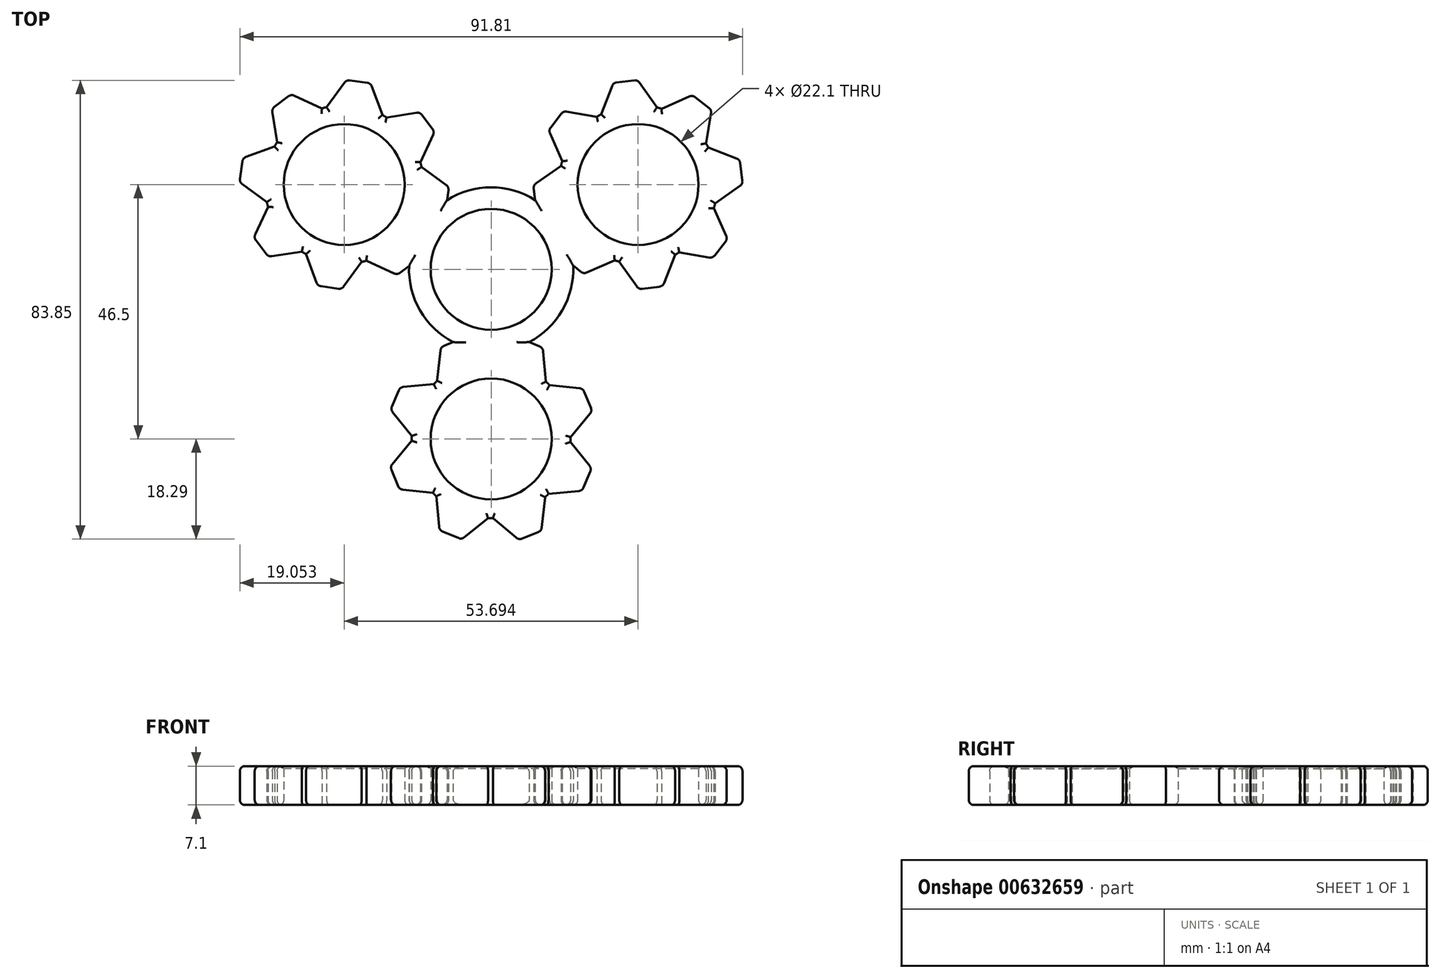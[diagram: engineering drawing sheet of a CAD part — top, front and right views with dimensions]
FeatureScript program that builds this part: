
annotation { "Feature Type Name" : "Feature", "Feature Type Description" : "" }
export const myFeature = defineFeature(function(context is Context, id is Id, definition is map)
    precondition{}
    {
        {
            var Q0;
            Q0=qCreatedBy(makeId("Top.planeOp"),FACE);
            var sketch = newSketch(context, id + "F0", { "sketchPlane" : qUnion([Q0])});
            skCircle(sketch, "E0", {"center": v(0, 0) * mm, "radius": 11.05 * mm});
            skArc(sketch, "E1", {"start": v(6.93, -13.3) * mm, "mid": v(13, -7.5) * mm, "end": v(14.99, 0.66) * mm});
            skCircle(sketch, "E2", {"center": v(0, -31) * mm, "radius": 11.05 * mm});
            skLineSegment(sketch, "E3", {"start": v(0, -31) * mm, "end": v(7.42, -13.5) * mm, "construction": true});
            skLineSegment(sketch, "E4", {"start": v(10.02, -20.52) * mm, "end": v(9.51, -14.97) * mm});
            skLineSegment(sketch, "E5", {"start": v(0, 0) * mm, "end": v(0, -31) * mm, "construction": true});
            skArc(sketch, "E6", {"start": v(-9.85, -20.36) * mm, "mid": v(-10.17, -20.66) * mm, "end": v(-10.48, -20.98) * mm});
            skLineSegment(sketch, "E7", {"start": v(7.42, -13.5) * mm, "end": v(8.9, -14.14) * mm});
            skLineSegment(sketch, "E8.MirrorCS", {"start": v(7.42, -13.5) * mm, "end": v(6.93, -13.3) * mm});
            skPoint(sketch, "E9.visualSharp", {"position": v(5.37, -12.64) * mm});
            skPoint(sketch, "E10.visualSharp", {"position": v(9.46, -14.37) * mm});
            skArc(sketch, "E10.filletArc", {"start": v(9.51, -14.97) * mm, "mid": v(9.32, -14.47) * mm, "end": v(8.9, -14.14) * mm});
            skLineSegment(sketch, "E11.1.2", {"start": v(-7.13, -13.39) * mm, "end": v(-6.93, -13.3) * mm});
            skLineSegment(sketch, "E11.1.3", {"start": v(-7.13, -13.39) * mm, "end": v(-8.63, -14) * mm});
            skArc(sketch, "E11.1.4", {"start": v(-8.63, -14) * mm, "mid": v(-9.05, -14.32) * mm, "end": v(-9.25, -14.81) * mm});
            skLineSegment(sketch, "E11.1.5", {"start": v(-9.85, -20.36) * mm, "end": v(-9.25, -14.81) * mm});
            skLineSegment(sketch, "E11.2.0", {"start": v(-10.48, -20.98) * mm, "end": v(-16.03, -21.49) * mm});
            skArc(sketch, "E11.2.1", {"start": v(-16.03, -21.49) * mm, "mid": v(-16.53, -21.68) * mm, "end": v(-16.86, -22.1) * mm});
            skLineSegment(sketch, "E11.2.2", {"start": v(-17.5, -23.58) * mm, "end": v(-16.86, -22.1) * mm});
            skLineSegment(sketch, "E11.2.3", {"start": v(-17.5, -23.58) * mm, "end": v(-18.12, -25.07) * mm});
            skArc(sketch, "E11.2.4", {"start": v(-18.12, -25.07) * mm, "mid": v(-18.2, -25.6) * mm, "end": v(-17.98, -26.1) * mm});
            skLineSegment(sketch, "E11.2.5", {"start": v(-14.49, -30.44) * mm, "end": v(-17.98, -26.1) * mm});
            skLineSegment(sketch, "E11.3.0", {"start": v(-14.5, -31.32) * mm, "end": v(-18.06, -35.61) * mm});
            skArc(sketch, "E11.3.1", {"start": v(-18.06, -35.61) * mm, "mid": v(-18.28, -36.1) * mm, "end": v(-18.22, -36.62) * mm});
            skLineSegment(sketch, "E11.3.2", {"start": v(-17.61, -38.13) * mm, "end": v(-18.22, -36.62) * mm});
            skLineSegment(sketch, "E11.3.3", {"start": v(-17.61, -38.13) * mm, "end": v(-17, -39.63) * mm});
            skArc(sketch, "E11.3.4", {"start": v(-17, -39.63) * mm, "mid": v(-16.68, -40.05) * mm, "end": v(-16.19, -40.25) * mm});
            skLineSegment(sketch, "E11.3.5", {"start": v(-10.64, -40.85) * mm, "end": v(-16.19, -40.25) * mm});
            skLineSegment(sketch, "E11.4.0", {"start": v(-10.02, -41.48) * mm, "end": v(-9.51, -47.03) * mm});
            skArc(sketch, "E11.4.1", {"start": v(-9.51, -47.03) * mm, "mid": v(-9.32, -47.53) * mm, "end": v(-8.9, -47.86) * mm});
            skLineSegment(sketch, "E11.4.2", {"start": v(-7.42, -48.5) * mm, "end": v(-8.9, -47.86) * mm});
            skLineSegment(sketch, "E11.4.3", {"start": v(-7.42, -48.5) * mm, "end": v(-5.93, -49.12) * mm});
            skArc(sketch, "E11.4.4", {"start": v(-5.93, -49.12) * mm, "mid": v(-5.4, -49.2) * mm, "end": v(-4.9, -48.98) * mm});
            skLineSegment(sketch, "E11.4.5", {"start": v(-0.56, -45.49) * mm, "end": v(-4.9, -48.98) * mm});
            skLineSegment(sketch, "E11.5.0", {"start": v(0.32, -45.5) * mm, "end": v(4.61, -49.06) * mm});
            skArc(sketch, "E11.5.1", {"start": v(4.61, -49.06) * mm, "mid": v(5.1, -49.28) * mm, "end": v(5.62, -49.22) * mm});
            skLineSegment(sketch, "E11.5.2", {"start": v(7.13, -48.61) * mm, "end": v(5.62, -49.22) * mm});
            skLineSegment(sketch, "E11.5.3", {"start": v(7.13, -48.61) * mm, "end": v(8.63, -48) * mm});
            skArc(sketch, "E11.5.4", {"start": v(8.63, -48) * mm, "mid": v(9.05, -47.68) * mm, "end": v(9.25, -47.19) * mm});
            skLineSegment(sketch, "E11.5.5", {"start": v(9.85, -41.64) * mm, "end": v(9.25, -47.19) * mm});
            skLineSegment(sketch, "E11.6.0", {"start": v(10.48, -41.02) * mm, "end": v(16.03, -40.51) * mm});
            skArc(sketch, "E11.6.1", {"start": v(16.03, -40.51) * mm, "mid": v(16.53, -40.32) * mm, "end": v(16.86, -39.9) * mm});
            skLineSegment(sketch, "E11.6.2", {"start": v(17.5, -38.42) * mm, "end": v(16.86, -39.9) * mm});
            skLineSegment(sketch, "E11.6.3", {"start": v(17.5, -38.42) * mm, "end": v(18.12, -36.93) * mm});
            skArc(sketch, "E11.6.4", {"start": v(18.12, -36.93) * mm, "mid": v(18.2, -36.4) * mm, "end": v(17.98, -35.9) * mm});
            skLineSegment(sketch, "E11.6.5", {"start": v(14.49, -31.56) * mm, "end": v(17.98, -35.9) * mm});
            skLineSegment(sketch, "E11.7.0", {"start": v(14.5, -30.68) * mm, "end": v(18.06, -26.39) * mm});
            skArc(sketch, "E11.7.1", {"start": v(18.06, -26.39) * mm, "mid": v(18.28, -25.9) * mm, "end": v(18.22, -25.38) * mm});
            skLineSegment(sketch, "E11.7.2", {"start": v(17.61, -23.87) * mm, "end": v(18.22, -25.38) * mm});
            skLineSegment(sketch, "E11.7.3", {"start": v(17.61, -23.87) * mm, "end": v(17, -22.37) * mm});
            skArc(sketch, "E11.7.4", {"start": v(17, -22.37) * mm, "mid": v(16.68, -21.95) * mm, "end": v(16.19, -21.75) * mm});
            skLineSegment(sketch, "E11.7.5", {"start": v(10.64, -21.15) * mm, "end": v(16.19, -21.75) * mm});
            skPoint(sketch, "E12.orphan", {"position": v(0.56, -16.51) * mm});
            skPoint(sketch, "E13.orphan", {"position": v(-0.32, -16.5) * mm});
            skArc(sketch, "E14.trimOffspring", {"start": v(10.64, -21.15) * mm, "mid": v(10.34, -20.83) * mm, "end": v(10.02, -20.52) * mm});
            skArc(sketch, "E15.trimOffspring", {"start": v(14.49, -31.56) * mm, "mid": v(14.5, -31.12) * mm, "end": v(14.5, -30.68) * mm});
            skArc(sketch, "E16.trimOffspring", {"start": v(9.85, -41.64) * mm, "mid": v(10.17, -41.34) * mm, "end": v(10.48, -41.02) * mm});
            skArc(sketch, "E17.trimOffspring", {"start": v(-0.56, -45.49) * mm, "mid": v(-0.12, -45.5) * mm, "end": v(0.32, -45.5) * mm});
            skArc(sketch, "E18.trimOffspring", {"start": v(-10.64, -40.85) * mm, "mid": v(-10.34, -41.17) * mm, "end": v(-10.02, -41.48) * mm});
            skArc(sketch, "E19.trimOffspring", {"start": v(-14.49, -30.44) * mm, "mid": v(-14.5, -30.88) * mm, "end": v(-14.5, -31.32) * mm});
            skLineSegment(sketch, "E20.1.0", {"start": v(22.55, 1.65) * mm, "end": v(17.45, -0.6) * mm});
            skPoint(sketch, "E20.1.1", {"position": v(7.72, 15.38) * mm});
            skLineSegment(sketch, "E20.1.2", {"start": v(30.29, 29.59) * mm, "end": v(27.07, 34.14) * mm});
            skArc(sketch, "E20.1.3", {"start": v(13, 19.8) * mm, "mid": v(12.87, 19.37) * mm, "end": v(12.76, 18.94) * mm});
            skPoint(sketch, "E20.1.4", {"position": v(26.85, 15.5) * mm});
            skLineSegment(sketch, "E20.1.5", {"start": v(19.32, 27.9) * mm, "end": v(13.82, 28.84) * mm});
            skLineSegment(sketch, "E20.1.7", {"start": v(40.7, 11.2) * mm, "end": v(42.95, 6.1) * mm});
            skPoint(sketch, "E20.1.8", {"position": v(14.02, 8.74) * mm});
            skArc(sketch, "E20.1.9", {"start": v(39.68, 22.26) * mm, "mid": v(39.46, 22.65) * mm, "end": v(39.24, 23.03) * mm});
            skArc(sketch, "E20.1.10", {"start": v(20.09, 28.33) * mm, "mid": v(19.7, 28.12) * mm, "end": v(19.32, 27.9) * mm});
            skLineSegment(sketch, "E20.1.11", {"start": v(31.14, 29.35) * mm, "end": v(36.24, 31.6) * mm});
            skArc(sketch, "E20.1.12", {"start": v(22.55, 1.65) * mm, "mid": v(22.98, 1.53) * mm, "end": v(23.4, 1.41) * mm});
            skLineSegment(sketch, "E20.1.13", {"start": v(23.4, 1.41) * mm, "end": v(26.63, -3.14) * mm});
            skPoint(sketch, "E20.1.14", {"position": v(14.45, 7.97) * mm});
            skArc(sketch, "E20.1.15", {"start": v(31.14, 29.35) * mm, "mid": v(30.72, 29.47) * mm, "end": v(30.29, 29.59) * mm});
            skCircle(sketch, "E20.1.16", {"center": v(26.85, 15.5) * mm, "radius": 11.05 * mm});
            skLineSegment(sketch, "E20.1.18", {"start": v(40.93, 12.06) * mm, "end": v(45.49, 15.28) * mm});
            skLineSegment(sketch, "E20.1.19", {"start": v(13, 19.8) * mm, "end": v(10.75, 24.9) * mm});
            skArc(sketch, "E20.1.20", {"start": v(40.7, 11.2) * mm, "mid": v(40.82, 11.63) * mm, "end": v(40.93, 12.06) * mm});
            skLineSegment(sketch, "E20.1.21", {"start": v(12.76, 18.94) * mm, "end": v(8.2, 15.72) * mm});
            skArc(sketch, "E20.1.22", {"start": v(33.6, 2.67) * mm, "mid": v(34, 2.88) * mm, "end": v(34.38, 3.1) * mm});
            skPoint(sketch, "E20.1.23", {"position": v(26.85, 15.5) * mm});
            skArc(sketch, "E20.1.24", {"start": v(45.49, 15.28) * mm, "mid": v(45.82, 15.7) * mm, "end": v(45.9, 16.22) * mm});
            skArc(sketch, "E20.1.25", {"start": v(10.87, 25.91) * mm, "mid": v(10.67, 25.42) * mm, "end": v(10.75, 24.9) * mm});
            skLineSegment(sketch, "E20.1.26", {"start": v(41.82, 3.8) * mm, "end": v(42.82, 5.09) * mm});
            skArc(sketch, "E20.1.27", {"start": v(42.82, 5.09) * mm, "mid": v(43.02, 5.58) * mm, "end": v(42.95, 6.1) * mm});
            skLineSegment(sketch, "E20.1.28", {"start": v(20.09, 28.33) * mm, "end": v(22.1, 33.53) * mm});
            skLineSegment(sketch, "E20.1.29", {"start": v(34.38, 3.1) * mm, "end": v(39.87, 2.16) * mm});
            skArc(sketch, "E20.1.30", {"start": v(27.07, 34.14) * mm, "mid": v(26.66, 34.48) * mm, "end": v(26.13, 34.56) * mm});
            skLineSegment(sketch, "E20.1.31", {"start": v(33.6, 2.67) * mm, "end": v(31.59, -2.53) * mm});
            skArc(sketch, "E20.1.32", {"start": v(26.63, -3.14) * mm, "mid": v(27.04, -3.48) * mm, "end": v(27.56, -3.56) * mm});
            skLineSegment(sketch, "E20.1.33", {"start": v(29.17, -3.36) * mm, "end": v(27.56, -3.56) * mm});
            skLineSegment(sketch, "E20.1.34", {"start": v(15.16, 0.52) * mm, "end": v(16.43, -0.47) * mm});
            skArc(sketch, "E20.1.35", {"start": v(39.87, 2.16) * mm, "mid": v(40.4, 2.22) * mm, "end": v(40.83, 2.53) * mm});
            skLineSegment(sketch, "E20.1.36", {"start": v(45.7, 17.82) * mm, "end": v(45.5, 19.43) * mm});
            skLineSegment(sketch, "E20.1.37", {"start": v(41.82, 3.8) * mm, "end": v(40.83, 2.53) * mm});
            skLineSegment(sketch, "E20.1.38", {"start": v(29.17, -3.36) * mm, "end": v(30.78, -3.16) * mm});
            skLineSegment(sketch, "E20.1.39", {"start": v(24.52, 34.36) * mm, "end": v(26.13, 34.56) * mm});
            skLineSegment(sketch, "E20.1.40", {"start": v(11.87, 27.2) * mm, "end": v(12.87, 28.47) * mm});
            skArc(sketch, "E20.1.41", {"start": v(45.5, 19.43) * mm, "mid": v(45.3, 19.92) * mm, "end": v(44.88, 20.24) * mm});
            skArc(sketch, "E20.1.42", {"start": v(37.26, 31.47) * mm, "mid": v(36.77, 31.68) * mm, "end": v(36.24, 31.6) * mm});
            skArc(sketch, "E20.1.43", {"start": v(22.92, 34.16) * mm, "mid": v(22.42, 33.96) * mm, "end": v(22.1, 33.53) * mm});
            skLineSegment(sketch, "E20.1.44", {"start": v(45.7, 17.82) * mm, "end": v(45.9, 16.22) * mm});
            skArc(sketch, "E20.1.45", {"start": v(8.2, 15.72) * mm, "mid": v(7.87, 15.3) * mm, "end": v(7.8, 14.78) * mm});
            skLineSegment(sketch, "E20.1.46", {"start": v(39.24, 23.03) * mm, "end": v(40.18, 28.52) * mm});
            skLineSegment(sketch, "E20.1.47", {"start": v(38.54, 30.48) * mm, "end": v(37.26, 31.47) * mm});
            skArc(sketch, "E20.1.48", {"start": v(30.78, -3.16) * mm, "mid": v(31.27, -2.96) * mm, "end": v(31.59, -2.53) * mm});
            skLineSegment(sketch, "E20.1.49", {"start": v(38.54, 30.48) * mm, "end": v(39.81, 29.48) * mm});
            skPoint(sketch, "E20.1.50", {"position": v(8.26, 10.98) * mm});
            skLineSegment(sketch, "E20.1.51", {"start": v(24.52, 34.36) * mm, "end": v(22.92, 34.16) * mm});
            skArc(sketch, "E20.1.53", {"start": v(13.82, 28.84) * mm, "mid": v(13.3, 28.78) * mm, "end": v(12.87, 28.47) * mm});
            skArc(sketch, "E20.1.54", {"start": v(40.18, 28.52) * mm, "mid": v(40.13, 29.05) * mm, "end": v(39.81, 29.48) * mm});
            skArc(sketch, "E20.1.55", {"start": v(16.43, -0.47) * mm, "mid": v(16.92, -0.68) * mm, "end": v(17.45, -0.6) * mm});
            skLineSegment(sketch, "E20.1.56", {"start": v(39.68, 22.26) * mm, "end": v(44.88, 20.24) * mm});
            skLineSegment(sketch, "E20.1.57", {"start": v(11.87, 27.2) * mm, "end": v(10.87, 25.91) * mm});
            skLineSegment(sketch, "E20.1.59", {"start": v(15.16, 0.52) * mm, "end": v(14.99, 0.66) * mm});
            skLineSegment(sketch, "E20.1.62", {"start": v(7.99, 13.18) * mm, "end": v(7.8, 14.78) * mm});
            skLineSegment(sketch, "E20.1.63", {"start": v(7.99, 13.18) * mm, "end": v(8.05, 12.65) * mm});
            skLineSegment(sketch, "E20.2.0", {"start": v(-12.7, 18.7) * mm, "end": v(-8.2, 15.41) * mm});
            skPoint(sketch, "E20.2.1", {"position": v(-17.18, -1) * mm});
            skLineSegment(sketch, "E20.2.2", {"start": v(-40.77, 11.44) * mm, "end": v(-43.1, 6.37) * mm});
            skArc(sketch, "E20.2.3", {"start": v(-23.64, 1.36) * mm, "mid": v(-23.2, 1.46) * mm, "end": v(-22.78, 1.58) * mm});
            skPoint(sketch, "E20.2.4", {"position": v(-26.85, 15.5) * mm});
            skLineSegment(sketch, "E20.2.5", {"start": v(-33.81, 2.78) * mm, "end": v(-31.89, -2.45) * mm});
            skLineSegment(sketch, "E20.2.7", {"start": v(-30.05, 29.64) * mm, "end": v(-26.76, 34.14) * mm});
            skPoint(sketch, "E20.2.8", {"position": v(-14.58, 7.77) * mm});
            skArc(sketch, "E20.2.9", {"start": v(-39.11, 23.23) * mm, "mid": v(-39.34, 22.85) * mm, "end": v(-39.56, 22.47) * mm});
            skArc(sketch, "E20.2.10", {"start": v(-34.58, 3.23) * mm, "mid": v(-34.2, 3) * mm, "end": v(-33.81, 2.78) * mm});
            skLineSegment(sketch, "E20.2.11", {"start": v(-40.99, 12.3) * mm, "end": v(-45.49, 15.59) * mm});
            skArc(sketch, "E20.2.12", {"start": v(-12.7, 18.7) * mm, "mid": v(-12.81, 19.14) * mm, "end": v(-12.93, 19.56) * mm});
            skLineSegment(sketch, "E20.2.13", {"start": v(-12.93, 19.56) * mm, "end": v(-10.6, 24.63) * mm});
            skPoint(sketch, "E20.2.14", {"position": v(-14.13, 8.53) * mm});
            skArc(sketch, "E20.2.15", {"start": v(-40.99, 12.3) * mm, "mid": v(-40.88, 11.86) * mm, "end": v(-40.77, 11.44) * mm});
            skCircle(sketch, "E20.2.16", {"center": v(-26.85, 15.5) * mm, "radius": 11.05 * mm});
            skLineSegment(sketch, "E20.2.18", {"start": v(-30.91, 29.42) * mm, "end": v(-35.97, 31.75) * mm});
            skLineSegment(sketch, "E20.2.19", {"start": v(-23.64, 1.36) * mm, "end": v(-26.93, -3.14) * mm});
            skArc(sketch, "E20.2.20", {"start": v(-30.05, 29.64) * mm, "mid": v(-30.48, 29.54) * mm, "end": v(-30.91, 29.42) * mm});
            skLineSegment(sketch, "E20.2.21", {"start": v(-22.78, 1.58) * mm, "end": v(-17.72, -0.75) * mm});
            skArc(sketch, "E20.2.22", {"start": v(-19.11, 27.77) * mm, "mid": v(-19.5, 28) * mm, "end": v(-19.88, 28.22) * mm});
            skPoint(sketch, "E20.2.23", {"position": v(-26.85, 15.5) * mm});
            skArc(sketch, "E20.2.24", {"start": v(-35.97, 31.75) * mm, "mid": v(-36.5, 31.84) * mm, "end": v(-37, 31.64) * mm});
            skArc(sketch, "E20.2.25", {"start": v(-27.88, -3.54) * mm, "mid": v(-27.35, -3.47) * mm, "end": v(-26.93, -3.14) * mm});
            skLineSegment(sketch, "E20.2.26", {"start": v(-24.21, 34.32) * mm, "end": v(-25.81, 34.54) * mm});
            skArc(sketch, "E20.2.27", {"start": v(-25.81, 34.54) * mm, "mid": v(-26.34, 34.47) * mm, "end": v(-26.76, 34.14) * mm});
            skLineSegment(sketch, "E20.2.28", {"start": v(-34.58, 3.23) * mm, "end": v(-40.09, 2.38) * mm});
            skLineSegment(sketch, "E20.2.29", {"start": v(-19.88, 28.22) * mm, "end": v(-21.8, 33.45) * mm});
            skArc(sketch, "E20.2.30", {"start": v(-43.1, 6.37) * mm, "mid": v(-43.19, 5.85) * mm, "end": v(-43, 5.35) * mm});
            skLineSegment(sketch, "E20.2.31", {"start": v(-19.11, 27.77) * mm, "end": v(-13.6, 28.62) * mm});
            skArc(sketch, "E20.2.32", {"start": v(-10.6, 24.63) * mm, "mid": v(-10.5, 25.15) * mm, "end": v(-10.7, 25.65) * mm});
            skLineSegment(sketch, "E20.2.33", {"start": v(-11.68, 26.94) * mm, "end": v(-10.7, 25.65) * mm});
            skLineSegment(sketch, "E20.2.34", {"start": v(-8.03, 12.86) * mm, "end": v(-7.8, 14.47) * mm});
            skArc(sketch, "E20.2.35", {"start": v(-21.8, 33.45) * mm, "mid": v(-22.12, 33.88) * mm, "end": v(-22.6, 34.1) * mm});
            skLineSegment(sketch, "E20.2.36", {"start": v(-38.29, 30.67) * mm, "end": v(-39.58, 29.7) * mm});
            skLineSegment(sketch, "E20.2.37", {"start": v(-24.21, 34.32) * mm, "end": v(-22.6, 34.1) * mm});
            skLineSegment(sketch, "E20.2.38", {"start": v(-11.68, 26.94) * mm, "end": v(-12.65, 28.23) * mm});
            skLineSegment(sketch, "E20.2.39", {"start": v(-42.02, 4.06) * mm, "end": v(-43, 5.35) * mm});
            skLineSegment(sketch, "E20.2.40", {"start": v(-29.48, -3.32) * mm, "end": v(-31.09, -3.1) * mm});
            skArc(sketch, "E20.2.41", {"start": v(-39.58, 29.7) * mm, "mid": v(-39.9, 29.27) * mm, "end": v(-39.97, 28.74) * mm});
            skArc(sketch, "E20.2.42", {"start": v(-45.89, 16.53) * mm, "mid": v(-45.82, 16) * mm, "end": v(-45.49, 15.59) * mm});
            skArc(sketch, "E20.2.43", {"start": v(-41.04, 2.77) * mm, "mid": v(-40.62, 2.44) * mm, "end": v(-40.09, 2.38) * mm});
            skLineSegment(sketch, "E20.2.44", {"start": v(-38.29, 30.67) * mm, "end": v(-37, 31.64) * mm});
            skArc(sketch, "E20.2.45", {"start": v(-17.72, -0.75) * mm, "mid": v(-17.2, -0.84) * mm, "end": v(-16.7, -0.64) * mm});
            skLineSegment(sketch, "E20.2.46", {"start": v(-39.56, 22.47) * mm, "end": v(-44.8, 20.54) * mm});
            skLineSegment(sketch, "E20.2.47", {"start": v(-45.66, 18.14) * mm, "end": v(-45.89, 16.53) * mm});
            skArc(sketch, "E20.2.48", {"start": v(-12.65, 28.23) * mm, "mid": v(-13.08, 28.56) * mm, "end": v(-13.6, 28.62) * mm});
            skLineSegment(sketch, "E20.2.49", {"start": v(-45.66, 18.14) * mm, "end": v(-45.44, 19.74) * mm});
            skPoint(sketch, "E20.2.50", {"position": v(-13.64, 1.67) * mm});
            skLineSegment(sketch, "E20.2.51", {"start": v(-42.02, 4.06) * mm, "end": v(-41.04, 2.77) * mm});
            skArc(sketch, "E20.2.53", {"start": v(-31.89, -2.45) * mm, "mid": v(-31.57, -2.88) * mm, "end": v(-31.09, -3.1) * mm});
            skArc(sketch, "E20.2.54", {"start": v(-44.8, 20.54) * mm, "mid": v(-45.23, 20.23) * mm, "end": v(-45.44, 19.74) * mm});
            skArc(sketch, "E20.2.55", {"start": v(-7.8, 14.47) * mm, "mid": v(-7.88, 15) * mm, "end": v(-8.2, 15.41) * mm});
            skLineSegment(sketch, "E20.2.56", {"start": v(-39.11, 23.23) * mm, "end": v(-39.97, 28.74) * mm});
            skLineSegment(sketch, "E20.2.57", {"start": v(-29.48, -3.32) * mm, "end": v(-27.88, -3.54) * mm});
            skLineSegment(sketch, "E20.2.59", {"start": v(-8.03, 12.86) * mm, "end": v(-8.06, 12.65) * mm});
            skLineSegment(sketch, "E20.2.62", {"start": v(-15.4, 0.33) * mm, "end": v(-16.7, -0.64) * mm});
            skLineSegment(sketch, "E20.2.63", {"start": v(-15.4, 0.33) * mm, "end": v(-14.99, 0.65) * mm});
            skArc(sketch, "E21.trimOffspring", {"start": v(-14.99, 0.65) * mm, "mid": v(-12.99, -7.5) * mm, "end": v(-6.93, -13.3) * mm});
            skArc(sketch, "E22.trimOffspring", {"start": v(8.05, 12.65) * mm, "mid": v(0, 15) * mm, "end": v(-8.06, 12.65) * mm});
            skPoint(sketch, "E23.start.orphan", {"position": v(-4, -14.46) * mm});
            skPoint(sketch, "E24.orphan", {"position": v(4, -14.46) * mm});
            skPoint(sketch, "E9.filletArc.end.orphan", {"position": v(4.9, -13.02) * mm});
            skPoint(sketch, "E25.orphan", {"position": v(-8.26, 11.26) * mm});
            skPoint(sketch, "E26.orphan", {"position": v(-14.11, 1.3) * mm});
            skSolve(sketch);
        }
        {
            var Q0;
            Q0=makeQuery(id+"F0.imprint","IMPRINT",FACE,{"disambiguationData":[TD([[makeQuery(id+"F0.imprint","IMPRINT",EDGE,{"derivedFrom":sQuery(id+"F0.wireOp",EDGE,"E0")}),-1.0]])]});
            extrude(context, id + "F1", {"entities" : qUnion([Q0]), "depth" : 7.1 * mm, "offsetDistance" : 25 * mm});
        }
        {
            var Q0;
            Q0=makeQuery(id+"F1.opExtrude","CAP_EDGE",EDGE,{"disambiguationData":[OSD([sQuery(id+"F0.wireOp",EDGE,"E20.2.16")])],"isStart":false});
            var Q1;
            Q1=makeQuery(id+"F1.opExtrude","CAP_EDGE",EDGE,{"disambiguationData":[OSD([sQuery(id+"F0.wireOp",EDGE,"E0")])],"isStart":false});
            var Q2;
            Q2=makeQuery(id+"F1.opExtrude","CAP_EDGE",EDGE,{"disambiguationData":[OSD([sQuery(id+"F0.wireOp",EDGE,"E20.1.16")])],"isStart":false});
            var Q3;
            Q3=makeQuery(id+"F1.opExtrude","CAP_EDGE",EDGE,{"disambiguationData":[OSD([sQuery(id+"F0.wireOp",EDGE,"E2")])],"isStart":false});
            chamfer(context, id + "F2", {"entities" : qUnion([Q0, Q1, Q2, Q3]), "width" : .5 * mm, "tangentPropagation" : true});
        }
        {
            var Q0;
            Q0=makeQuery(id+"F1.opExtrude","CAP_FACE",FACE,{"disambiguationData":[OSD([sQuery(id+"F0.wireOp",EDGE,"E0"),sQuery(id+"F0.wireOp",EDGE,"E1"),sQuery(id+"F0.wireOp",EDGE,"E2"),sQuery(id+"F0.wireOp",EDGE,"E4"),sQuery(id+"F0.wireOp",EDGE,"E6"),sQuery(id+"F0.wireOp",EDGE,"E7"),sQuery(id+"F0.wireOp",EDGE,"E8.MirrorCS"),sQuery(id+"F0.wireOp",EDGE,"E10.filletArc"),sQuery(id+"F0.wireOp",EDGE,"E11.1.2"),sQuery(id+"F0.wireOp",EDGE,"E11.1.3"),sQuery(id+"F0.wireOp",EDGE,"E11.1.4"),sQuery(id+"F0.wireOp",EDGE,"E11.1.5"),sQuery(id+"F0.wireOp",EDGE,"E11.2.0"),sQuery(id+"F0.wireOp",EDGE,"E11.2.1"),sQuery(id+"F0.wireOp",EDGE,"E11.2.2"),sQuery(id+"F0.wireOp",EDGE,"E11.2.3"),sQuery(id+"F0.wireOp",EDGE,"E11.2.4"),sQuery(id+"F0.wireOp",EDGE,"E11.2.5"),sQuery(id+"F0.wireOp",EDGE,"E11.3.0"),sQuery(id+"F0.wireOp",EDGE,"E11.3.1"),sQuery(id+"F0.wireOp",EDGE,"E11.3.2"),sQuery(id+"F0.wireOp",EDGE,"E11.3.3"),sQuery(id+"F0.wireOp",EDGE,"E11.3.4"),sQuery(id+"F0.wireOp",EDGE,"E11.3.5"),sQuery(id+"F0.wireOp",EDGE,"E11.4.0"),sQuery(id+"F0.wireOp",EDGE,"E11.4.1"),sQuery(id+"F0.wireOp",EDGE,"E11.4.2"),sQuery(id+"F0.wireOp",EDGE,"E11.4.3"),sQuery(id+"F0.wireOp",EDGE,"E11.4.4"),sQuery(id+"F0.wireOp",EDGE,"E11.4.5"),sQuery(id+"F0.wireOp",EDGE,"E11.5.0"),sQuery(id+"F0.wireOp",EDGE,"E11.5.1"),sQuery(id+"F0.wireOp",EDGE,"E11.5.2"),sQuery(id+"F0.wireOp",EDGE,"E11.5.3"),sQuery(id+"F0.wireOp",EDGE,"E11.5.4"),sQuery(id+"F0.wireOp",EDGE,"E11.5.5"),sQuery(id+"F0.wireOp",EDGE,"E11.6.0"),sQuery(id+"F0.wireOp",EDGE,"E11.6.1"),sQuery(id+"F0.wireOp",EDGE,"E11.6.2"),sQuery(id+"F0.wireOp",EDGE,"E11.6.3"),sQuery(id+"F0.wireOp",EDGE,"E11.6.4"),sQuery(id+"F0.wireOp",EDGE,"E11.6.5"),sQuery(id+"F0.wireOp",EDGE,"E11.7.0"),sQuery(id+"F0.wireOp",EDGE,"E11.7.1"),sQuery(id+"F0.wireOp",EDGE,"E11.7.2"),sQuery(id+"F0.wireOp",EDGE,"E11.7.3"),sQuery(id+"F0.wireOp",EDGE,"E11.7.4"),sQuery(id+"F0.wireOp",EDGE,"E11.7.5"),sQuery(id+"F0.wireOp",EDGE,"E14.trimOffspring"),sQuery(id+"F0.wireOp",EDGE,"E15.trimOffspring"),sQuery(id+"F0.wireOp",EDGE,"E16.trimOffspring"),sQuery(id+"F0.wireOp",EDGE,"E17.trimOffspring"),sQuery(id+"F0.wireOp",EDGE,"E18.trimOffspring"),sQuery(id+"F0.wireOp",EDGE,"E19.trimOffspring"),sQuery(id+"F0.wireOp",EDGE,"E20.1.0"),sQuery(id+"F0.wireOp",EDGE,"E20.1.2"),sQuery(id+"F0.wireOp",EDGE,"E20.1.3"),sQuery(id+"F0.wireOp",EDGE,"E20.1.5"),sQuery(id+"F0.wireOp",EDGE,"E20.1.7"),sQuery(id+"F0.wireOp",EDGE,"E20.1.9"),sQuery(id+"F0.wireOp",EDGE,"E20.1.10"),sQuery(id+"F0.wireOp",EDGE,"E20.1.11"),sQuery(id+"F0.wireOp",EDGE,"E20.1.12"),sQuery(id+"F0.wireOp",EDGE,"E20.1.13"),sQuery(id+"F0.wireOp",EDGE,"E20.1.15"),sQuery(id+"F0.wireOp",EDGE,"E20.1.16"),sQuery(id+"F0.wireOp",EDGE,"E20.1.18"),sQuery(id+"F0.wireOp",EDGE,"E20.1.19"),sQuery(id+"F0.wireOp",EDGE,"E20.1.20"),sQuery(id+"F0.wireOp",EDGE,"E20.1.21"),sQuery(id+"F0.wireOp",EDGE,"E20.1.22"),sQuery(id+"F0.wireOp",EDGE,"E20.1.24"),sQuery(id+"F0.wireOp",EDGE,"E20.1.25"),sQuery(id+"F0.wireOp",EDGE,"E20.1.26"),sQuery(id+"F0.wireOp",EDGE,"E20.1.27"),sQuery(id+"F0.wireOp",EDGE,"E20.1.28"),sQuery(id+"F0.wireOp",EDGE,"E20.1.29"),sQuery(id+"F0.wireOp",EDGE,"E20.1.30"),sQuery(id+"F0.wireOp",EDGE,"E20.1.31"),sQuery(id+"F0.wireOp",EDGE,"E20.1.32"),sQuery(id+"F0.wireOp",EDGE,"E20.1.33"),sQuery(id+"F0.wireOp",EDGE,"E20.1.34"),sQuery(id+"F0.wireOp",EDGE,"E20.1.35"),sQuery(id+"F0.wireOp",EDGE,"E20.1.36"),sQuery(id+"F0.wireOp",EDGE,"E20.1.37"),sQuery(id+"F0.wireOp",EDGE,"E20.1.38"),sQuery(id+"F0.wireOp",EDGE,"E20.1.39"),sQuery(id+"F0.wireOp",EDGE,"E20.1.40"),sQuery(id+"F0.wireOp",EDGE,"E20.1.41"),sQuery(id+"F0.wireOp",EDGE,"E20.1.42"),sQuery(id+"F0.wireOp",EDGE,"E20.1.43"),sQuery(id+"F0.wireOp",EDGE,"E20.1.44"),sQuery(id+"F0.wireOp",EDGE,"E20.1.45"),sQuery(id+"F0.wireOp",EDGE,"E20.1.46"),sQuery(id+"F0.wireOp",EDGE,"E20.1.47"),sQuery(id+"F0.wireOp",EDGE,"E20.1.48"),sQuery(id+"F0.wireOp",EDGE,"E20.1.49"),sQuery(id+"F0.wireOp",EDGE,"E20.1.51"),sQuery(id+"F0.wireOp",EDGE,"E20.1.53"),sQuery(id+"F0.wireOp",EDGE,"E20.1.54"),sQuery(id+"F0.wireOp",EDGE,"E20.1.55"),sQuery(id+"F0.wireOp",EDGE,"E20.1.56"),sQuery(id+"F0.wireOp",EDGE,"E20.1.57"),sQuery(id+"F0.wireOp",EDGE,"E20.1.59"),sQuery(id+"F0.wireOp",EDGE,"E20.1.62"),sQuery(id+"F0.wireOp",EDGE,"E20.1.63"),sQuery(id+"F0.wireOp",EDGE,"E20.2.0"),sQuery(id+"F0.wireOp",EDGE,"E20.2.2"),sQuery(id+"F0.wireOp",EDGE,"E20.2.3"),sQuery(id+"F0.wireOp",EDGE,"E20.2.5"),sQuery(id+"F0.wireOp",EDGE,"E20.2.7"),sQuery(id+"F0.wireOp",EDGE,"E20.2.9"),sQuery(id+"F0.wireOp",EDGE,"E20.2.10"),sQuery(id+"F0.wireOp",EDGE,"E20.2.11"),sQuery(id+"F0.wireOp",EDGE,"E20.2.12"),sQuery(id+"F0.wireOp",EDGE,"E20.2.13"),sQuery(id+"F0.wireOp",EDGE,"E20.2.15"),sQuery(id+"F0.wireOp",EDGE,"E20.2.16"),sQuery(id+"F0.wireOp",EDGE,"E20.2.18"),sQuery(id+"F0.wireOp",EDGE,"E20.2.19"),sQuery(id+"F0.wireOp",EDGE,"E20.2.20"),sQuery(id+"F0.wireOp",EDGE,"E20.2.21"),sQuery(id+"F0.wireOp",EDGE,"E20.2.22"),sQuery(id+"F0.wireOp",EDGE,"E20.2.24"),sQuery(id+"F0.wireOp",EDGE,"E20.2.25"),sQuery(id+"F0.wireOp",EDGE,"E20.2.26"),sQuery(id+"F0.wireOp",EDGE,"E20.2.27"),sQuery(id+"F0.wireOp",EDGE,"E20.2.28"),sQuery(id+"F0.wireOp",EDGE,"E20.2.29"),sQuery(id+"F0.wireOp",EDGE,"E20.2.30"),sQuery(id+"F0.wireOp",EDGE,"E20.2.31"),sQuery(id+"F0.wireOp",EDGE,"E20.2.32"),sQuery(id+"F0.wireOp",EDGE,"E20.2.33"),sQuery(id+"F0.wireOp",EDGE,"E20.2.34"),sQuery(id+"F0.wireOp",EDGE,"E20.2.35"),sQuery(id+"F0.wireOp",EDGE,"E20.2.36"),sQuery(id+"F0.wireOp",EDGE,"E20.2.37"),sQuery(id+"F0.wireOp",EDGE,"E20.2.38"),sQuery(id+"F0.wireOp",EDGE,"E20.2.39"),sQuery(id+"F0.wireOp",EDGE,"E20.2.40"),sQuery(id+"F0.wireOp",EDGE,"E20.2.41"),sQuery(id+"F0.wireOp",EDGE,"E20.2.42"),sQuery(id+"F0.wireOp",EDGE,"E20.2.43"),sQuery(id+"F0.wireOp",EDGE,"E20.2.44"),sQuery(id+"F0.wireOp",EDGE,"E20.2.45"),sQuery(id+"F0.wireOp",EDGE,"E20.2.46"),sQuery(id+"F0.wireOp",EDGE,"E20.2.47"),sQuery(id+"F0.wireOp",EDGE,"E20.2.48"),sQuery(id+"F0.wireOp",EDGE,"E20.2.49"),sQuery(id+"F0.wireOp",EDGE,"E20.2.51"),sQuery(id+"F0.wireOp",EDGE,"E20.2.53"),sQuery(id+"F0.wireOp",EDGE,"E20.2.54"),sQuery(id+"F0.wireOp",EDGE,"E20.2.55"),sQuery(id+"F0.wireOp",EDGE,"E20.2.56"),sQuery(id+"F0.wireOp",EDGE,"E20.2.57"),sQuery(id+"F0.wireOp",EDGE,"E20.2.59"),sQuery(id+"F0.wireOp",EDGE,"E20.2.62"),sQuery(id+"F0.wireOp",EDGE,"E20.2.63"),sQuery(id+"F0.wireOp",EDGE,"E21.trimOffspring"),sQuery(id+"F0.wireOp",EDGE,"E22.trimOffspring")])],"isStart":false});
            var Q1;
            Q1=makeQuery(id+"F1.opExtrude","CAP_FACE",FACE,{"disambiguationData":[OSD([sQuery(id+"F0.wireOp",EDGE,"E0"),sQuery(id+"F0.wireOp",EDGE,"E1"),sQuery(id+"F0.wireOp",EDGE,"E2"),sQuery(id+"F0.wireOp",EDGE,"E4"),sQuery(id+"F0.wireOp",EDGE,"E6"),sQuery(id+"F0.wireOp",EDGE,"E7"),sQuery(id+"F0.wireOp",EDGE,"E8.MirrorCS"),sQuery(id+"F0.wireOp",EDGE,"E10.filletArc"),sQuery(id+"F0.wireOp",EDGE,"E11.1.2"),sQuery(id+"F0.wireOp",EDGE,"E11.1.3"),sQuery(id+"F0.wireOp",EDGE,"E11.1.4"),sQuery(id+"F0.wireOp",EDGE,"E11.1.5"),sQuery(id+"F0.wireOp",EDGE,"E11.2.0"),sQuery(id+"F0.wireOp",EDGE,"E11.2.1"),sQuery(id+"F0.wireOp",EDGE,"E11.2.2"),sQuery(id+"F0.wireOp",EDGE,"E11.2.3"),sQuery(id+"F0.wireOp",EDGE,"E11.2.4"),sQuery(id+"F0.wireOp",EDGE,"E11.2.5"),sQuery(id+"F0.wireOp",EDGE,"E11.3.0"),sQuery(id+"F0.wireOp",EDGE,"E11.3.1"),sQuery(id+"F0.wireOp",EDGE,"E11.3.2"),sQuery(id+"F0.wireOp",EDGE,"E11.3.3"),sQuery(id+"F0.wireOp",EDGE,"E11.3.4"),sQuery(id+"F0.wireOp",EDGE,"E11.3.5"),sQuery(id+"F0.wireOp",EDGE,"E11.4.0"),sQuery(id+"F0.wireOp",EDGE,"E11.4.1"),sQuery(id+"F0.wireOp",EDGE,"E11.4.2"),sQuery(id+"F0.wireOp",EDGE,"E11.4.3"),sQuery(id+"F0.wireOp",EDGE,"E11.4.4"),sQuery(id+"F0.wireOp",EDGE,"E11.4.5"),sQuery(id+"F0.wireOp",EDGE,"E11.5.0"),sQuery(id+"F0.wireOp",EDGE,"E11.5.1"),sQuery(id+"F0.wireOp",EDGE,"E11.5.2"),sQuery(id+"F0.wireOp",EDGE,"E11.5.3"),sQuery(id+"F0.wireOp",EDGE,"E11.5.4"),sQuery(id+"F0.wireOp",EDGE,"E11.5.5"),sQuery(id+"F0.wireOp",EDGE,"E11.6.0"),sQuery(id+"F0.wireOp",EDGE,"E11.6.1"),sQuery(id+"F0.wireOp",EDGE,"E11.6.2"),sQuery(id+"F0.wireOp",EDGE,"E11.6.3"),sQuery(id+"F0.wireOp",EDGE,"E11.6.4"),sQuery(id+"F0.wireOp",EDGE,"E11.6.5"),sQuery(id+"F0.wireOp",EDGE,"E11.7.0"),sQuery(id+"F0.wireOp",EDGE,"E11.7.1"),sQuery(id+"F0.wireOp",EDGE,"E11.7.2"),sQuery(id+"F0.wireOp",EDGE,"E11.7.3"),sQuery(id+"F0.wireOp",EDGE,"E11.7.4"),sQuery(id+"F0.wireOp",EDGE,"E11.7.5"),sQuery(id+"F0.wireOp",EDGE,"E14.trimOffspring"),sQuery(id+"F0.wireOp",EDGE,"E15.trimOffspring"),sQuery(id+"F0.wireOp",EDGE,"E16.trimOffspring"),sQuery(id+"F0.wireOp",EDGE,"E17.trimOffspring"),sQuery(id+"F0.wireOp",EDGE,"E18.trimOffspring"),sQuery(id+"F0.wireOp",EDGE,"E19.trimOffspring"),sQuery(id+"F0.wireOp",EDGE,"E20.1.0"),sQuery(id+"F0.wireOp",EDGE,"E20.1.2"),sQuery(id+"F0.wireOp",EDGE,"E20.1.3"),sQuery(id+"F0.wireOp",EDGE,"E20.1.5"),sQuery(id+"F0.wireOp",EDGE,"E20.1.7"),sQuery(id+"F0.wireOp",EDGE,"E20.1.9"),sQuery(id+"F0.wireOp",EDGE,"E20.1.10"),sQuery(id+"F0.wireOp",EDGE,"E20.1.11"),sQuery(id+"F0.wireOp",EDGE,"E20.1.12"),sQuery(id+"F0.wireOp",EDGE,"E20.1.13"),sQuery(id+"F0.wireOp",EDGE,"E20.1.15"),sQuery(id+"F0.wireOp",EDGE,"E20.1.16"),sQuery(id+"F0.wireOp",EDGE,"E20.1.18"),sQuery(id+"F0.wireOp",EDGE,"E20.1.19"),sQuery(id+"F0.wireOp",EDGE,"E20.1.20"),sQuery(id+"F0.wireOp",EDGE,"E20.1.21"),sQuery(id+"F0.wireOp",EDGE,"E20.1.22"),sQuery(id+"F0.wireOp",EDGE,"E20.1.24"),sQuery(id+"F0.wireOp",EDGE,"E20.1.25"),sQuery(id+"F0.wireOp",EDGE,"E20.1.26"),sQuery(id+"F0.wireOp",EDGE,"E20.1.27"),sQuery(id+"F0.wireOp",EDGE,"E20.1.28"),sQuery(id+"F0.wireOp",EDGE,"E20.1.29"),sQuery(id+"F0.wireOp",EDGE,"E20.1.30"),sQuery(id+"F0.wireOp",EDGE,"E20.1.31"),sQuery(id+"F0.wireOp",EDGE,"E20.1.32"),sQuery(id+"F0.wireOp",EDGE,"E20.1.33"),sQuery(id+"F0.wireOp",EDGE,"E20.1.34"),sQuery(id+"F0.wireOp",EDGE,"E20.1.35"),sQuery(id+"F0.wireOp",EDGE,"E20.1.36"),sQuery(id+"F0.wireOp",EDGE,"E20.1.37"),sQuery(id+"F0.wireOp",EDGE,"E20.1.38"),sQuery(id+"F0.wireOp",EDGE,"E20.1.39"),sQuery(id+"F0.wireOp",EDGE,"E20.1.40"),sQuery(id+"F0.wireOp",EDGE,"E20.1.41"),sQuery(id+"F0.wireOp",EDGE,"E20.1.42"),sQuery(id+"F0.wireOp",EDGE,"E20.1.43"),sQuery(id+"F0.wireOp",EDGE,"E20.1.44"),sQuery(id+"F0.wireOp",EDGE,"E20.1.45"),sQuery(id+"F0.wireOp",EDGE,"E20.1.46"),sQuery(id+"F0.wireOp",EDGE,"E20.1.47"),sQuery(id+"F0.wireOp",EDGE,"E20.1.48"),sQuery(id+"F0.wireOp",EDGE,"E20.1.49"),sQuery(id+"F0.wireOp",EDGE,"E20.1.51"),sQuery(id+"F0.wireOp",EDGE,"E20.1.53"),sQuery(id+"F0.wireOp",EDGE,"E20.1.54"),sQuery(id+"F0.wireOp",EDGE,"E20.1.55"),sQuery(id+"F0.wireOp",EDGE,"E20.1.56"),sQuery(id+"F0.wireOp",EDGE,"E20.1.57"),sQuery(id+"F0.wireOp",EDGE,"E20.1.59"),sQuery(id+"F0.wireOp",EDGE,"E20.1.62"),sQuery(id+"F0.wireOp",EDGE,"E20.1.63"),sQuery(id+"F0.wireOp",EDGE,"E20.2.0"),sQuery(id+"F0.wireOp",EDGE,"E20.2.2"),sQuery(id+"F0.wireOp",EDGE,"E20.2.3"),sQuery(id+"F0.wireOp",EDGE,"E20.2.5"),sQuery(id+"F0.wireOp",EDGE,"E20.2.7"),sQuery(id+"F0.wireOp",EDGE,"E20.2.9"),sQuery(id+"F0.wireOp",EDGE,"E20.2.10"),sQuery(id+"F0.wireOp",EDGE,"E20.2.11"),sQuery(id+"F0.wireOp",EDGE,"E20.2.12"),sQuery(id+"F0.wireOp",EDGE,"E20.2.13"),sQuery(id+"F0.wireOp",EDGE,"E20.2.15"),sQuery(id+"F0.wireOp",EDGE,"E20.2.16"),sQuery(id+"F0.wireOp",EDGE,"E20.2.18"),sQuery(id+"F0.wireOp",EDGE,"E20.2.19"),sQuery(id+"F0.wireOp",EDGE,"E20.2.20"),sQuery(id+"F0.wireOp",EDGE,"E20.2.21"),sQuery(id+"F0.wireOp",EDGE,"E20.2.22"),sQuery(id+"F0.wireOp",EDGE,"E20.2.24"),sQuery(id+"F0.wireOp",EDGE,"E20.2.25"),sQuery(id+"F0.wireOp",EDGE,"E20.2.26"),sQuery(id+"F0.wireOp",EDGE,"E20.2.27"),sQuery(id+"F0.wireOp",EDGE,"E20.2.28"),sQuery(id+"F0.wireOp",EDGE,"E20.2.29"),sQuery(id+"F0.wireOp",EDGE,"E20.2.30"),sQuery(id+"F0.wireOp",EDGE,"E20.2.31"),sQuery(id+"F0.wireOp",EDGE,"E20.2.32"),sQuery(id+"F0.wireOp",EDGE,"E20.2.33"),sQuery(id+"F0.wireOp",EDGE,"E20.2.34"),sQuery(id+"F0.wireOp",EDGE,"E20.2.35"),sQuery(id+"F0.wireOp",EDGE,"E20.2.36"),sQuery(id+"F0.wireOp",EDGE,"E20.2.37"),sQuery(id+"F0.wireOp",EDGE,"E20.2.38"),sQuery(id+"F0.wireOp",EDGE,"E20.2.39"),sQuery(id+"F0.wireOp",EDGE,"E20.2.40"),sQuery(id+"F0.wireOp",EDGE,"E20.2.41"),sQuery(id+"F0.wireOp",EDGE,"E20.2.42"),sQuery(id+"F0.wireOp",EDGE,"E20.2.43"),sQuery(id+"F0.wireOp",EDGE,"E20.2.44"),sQuery(id+"F0.wireOp",EDGE,"E20.2.45"),sQuery(id+"F0.wireOp",EDGE,"E20.2.46"),sQuery(id+"F0.wireOp",EDGE,"E20.2.47"),sQuery(id+"F0.wireOp",EDGE,"E20.2.48"),sQuery(id+"F0.wireOp",EDGE,"E20.2.49"),sQuery(id+"F0.wireOp",EDGE,"E20.2.51"),sQuery(id+"F0.wireOp",EDGE,"E20.2.53"),sQuery(id+"F0.wireOp",EDGE,"E20.2.54"),sQuery(id+"F0.wireOp",EDGE,"E20.2.55"),sQuery(id+"F0.wireOp",EDGE,"E20.2.56"),sQuery(id+"F0.wireOp",EDGE,"E20.2.57"),sQuery(id+"F0.wireOp",EDGE,"E20.2.59"),sQuery(id+"F0.wireOp",EDGE,"E20.2.62"),sQuery(id+"F0.wireOp",EDGE,"E20.2.63"),sQuery(id+"F0.wireOp",EDGE,"E21.trimOffspring"),sQuery(id+"F0.wireOp",EDGE,"E22.trimOffspring")])],"isStart":true});
            fillet(context, id + "F3", {"entities" : qUnion([Q0, Q1]), "radius" : .9 * mm, "tangentPropagation" : true, "allowEdgeOverflow" : false});
        }
    });
